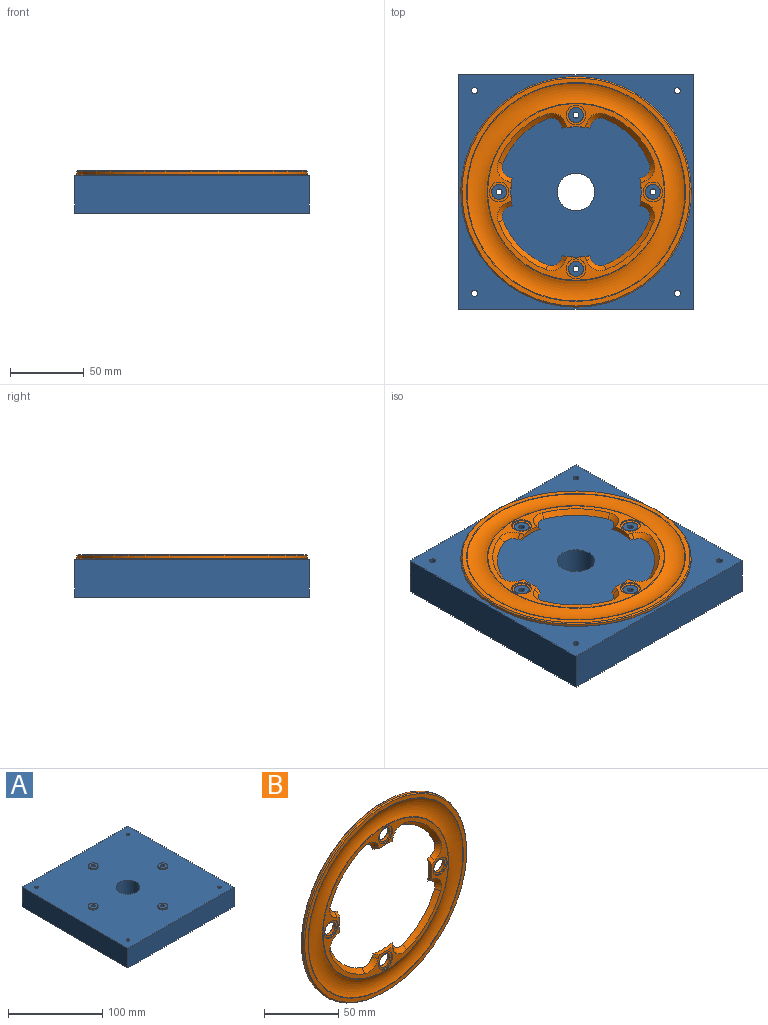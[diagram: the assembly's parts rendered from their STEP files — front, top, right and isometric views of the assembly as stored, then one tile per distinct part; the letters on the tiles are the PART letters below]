
ASSEMBLY  parts=2 mates=1
PART A: 23 faces, bbox 158.8x158.8x27.3 mm
  f0: plane 158.75x25.4mm, normal (-1,0,0), area 4032.3mm2, adj f1,f3,f4,f5
  f1: plane 158.75x25.4mm, normal (0,-1,0), area 4032.3mm2, adj f0,f2,f4,f5
  f2: plane 158.75x25.4mm, normal (1,0,0), area 4032.3mm2, adj f1,f3,f4,f5
  f3: plane 158.75x25.4mm, normal (0,1,0), area 4032.3mm2, adj f0,f2,f4,f5
  f4: plane 158.75x158.75mm, normal (0,0,-1), area 24592.4mm2, adj f0,f1,f2,f3,f14,f15,f16,f17
  f5: plane 158.75x158.75mm, normal (0,0,1), area 24320.9mm2, adj f0,f1,f2,f3,f6,f8,f10,f12
  f6: cylinder r=5.07mm len=10.13mm, axis (0,0,-1), area 60.7mm2, adj f5,f7
  f7: plane 10.13x10.13mm, normal (0,0,1), area 67.9mm2, adj f6,f17
  f8: cylinder r=5.07mm len=10.13mm, axis (0,0,-1), area 60.7mm2, adj f5,f9
  f9: plane 10.13x10.13mm, normal (0,0,1), area 67.9mm2, adj f8,f16
  f10: cylinder r=5.07mm len=10.13mm, axis (0,0,-1), area 60.7mm2, adj f5,f11
  f11: plane 10.13x10.13mm, normal (0,0,1), area 67.9mm2, adj f10,f15
  f12: cylinder r=5.07mm len=10.13mm, axis (0,0,-1), area 60.7mm2, adj f5,f13
  f13: plane 10.13x10.13mm, normal (0,0,1), area 67.9mm2, adj f12,f14
  f14: cylinder r=2.02mm len=27.31mm, axis (0,0,1), area 346.4mm2, adj f4,f13
  f15: cylinder r=2.02mm len=27.31mm, axis (0,0,1), area 346.4mm2, adj f4,f11
  f16: cylinder r=2.02mm len=27.31mm, axis (0,0,1), area 346.4mm2, adj f4,f9
  f17: cylinder r=2.02mm len=27.31mm, axis (0,0,1), area 346.4mm2, adj f4,f7
  f18: cylinder r=2.02mm len=25.4mm, axis (0,0,-1), area 322.3mm2, adj f4,f5
  f19: cylinder r=2.02mm len=25.4mm, axis (0,0,-1), area 322.3mm2, adj f4,f5
  f20: cylinder r=2.02mm len=25.4mm, axis (0,0,-1), area 322.3mm2, adj f4,f5
  f21: cylinder r=2.02mm len=25.4mm, axis (0,0,-1), area 322.3mm2, adj f4,f5
  f22: cylinder r=12.7mm len=25.4mm, axis (0,0,-1), area 2026.8mm2, adj f4,f5
PART B: 45 faces, bbox 168.7x6.1x168.7 mm
  f0: cylinder r=5.08mm len=10.16mm, axis (0,-1,0), area 72.2mm2, adj f6,f41
  f1: cylinder r=5.08mm len=10.16mm, axis (0,-1,0), area 72.2mm2, adj f6,f39
  f2: cylinder r=5.08mm len=10.16mm, axis (0,-1,0), area 72.2mm2, adj f6,f37
  f3: cylinder r=5.08mm len=10.16mm, axis (0,-1,0), area 72.2mm2, adj f6,f35
  f4: plane 154.31x154.31mm, normal (0,-1,0), area 1483.8mm2, adj f34,f44
  f5: plane 119.41x119.41mm, normal (0,-1,0), area 1629.6mm2, adj f8,f9,f10,f11,f13,f14,f15,f16
  f6: plane 154.31x154.31mm, normal (0,1,0), area 10363.6mm2, adj f0,f1,f2,f3,f8,f9,f10,f11
  f7: cylinder r=77.91mm len=155.83mm, axis (0,1,0), area 808.2mm2, adj f33,f34
  f8: cylinder r=44.13mm len=18.43mm, axis (0,-1,0), area 48.7mm2, adj f5,f6,f13,f32
  f9: cylinder r=44.13mm len=18.43mm, axis (0,-1,0), area 48.7mm2, adj f5,f6,f27,f28
  f10: cylinder r=44.13mm len=18.43mm, axis (0,-1,0), area 48.7mm2, adj f5,f6,f22,f23
  f11: cylinder r=44.13mm len=18.43mm, axis (0,-1,0), area 48.7mm2, adj f5,f6,f17,f18
  f12: torus R=66.87mm, axis (0,1,0), area 5939.5mm2, adj f43,f44
  f13: plane 4.02x3.4mm, normal (0.66,-0.71,-0.24), area 12.2mm2, adj f5,f6,f8,f14
  f14: cone r=6.35mm half-angle=45deg, axis (0,-1,0), area 61.2mm2, adj f5,f6,f13,f15
  f15: cone r=52.51mm half-angle=45deg, axis (0,-1,0), area 205.1mm2, adj f5,f6,f14,f16
  f16: cone r=10.16mm half-angle=45deg, axis (0,-1,0), area 61.2mm2, adj f5,f6,f15,f17
  f17: plane 4.02x3.4mm, normal (-0.24,-0.71,0.66), area 12.2mm2, adj f5,f6,f11,f16
  f18: plane 4.02x3.4mm, normal (-0.24,-0.71,-0.66), area 12.2mm2, adj f5,f6,f11,f19
  f19: cone r=6.35mm half-angle=45deg, axis (0,-1,0), area 61.2mm2, adj f5,f6,f18,f20
  f20: cone r=52.51mm half-angle=45deg, axis (0,-1,0), area 205.1mm2, adj f5,f6,f19,f21
  f21: cone r=10.16mm half-angle=45deg, axis (0,-1,0), area 61.2mm2, adj f5,f6,f20,f22
  f22: plane 4.02x3.4mm, normal (0.66,-0.71,0.24), area 12.2mm2, adj f5,f6,f10,f21
  f23: plane 4.02x3.4mm, normal (-0.66,-0.71,0.24), area 12.2mm2, adj f5,f6,f10,f24
  f24: cone r=6.35mm half-angle=45deg, axis (0,-1,0), area 61.2mm2, adj f5,f6,f23,f25
  f25: cone r=52.51mm half-angle=45deg, axis (0,-1,0), area 205.1mm2, adj f5,f6,f24,f26
  f26: cone r=10.16mm half-angle=45deg, axis (0,-1,0), area 61.2mm2, adj f5,f6,f25,f27
  f27: plane 4.02x3.4mm, normal (0.24,-0.71,-0.66), area 12.2mm2, adj f5,f6,f9,f26
  f28: plane 4.02x3.4mm, normal (0.24,-0.71,0.66), area 12.2mm2, adj f5,f6,f9,f29
  f29: cone r=6.35mm half-angle=45deg, axis (0,-1,0), area 61.2mm2, adj f5,f6,f28,f30
  f30: cone r=52.51mm half-angle=45deg, axis (0,-1,0), area 205.1mm2, adj f5,f6,f29,f31
  f31: cone r=10.16mm half-angle=45deg, axis (0,-1,0), area 61.2mm2, adj f5,f6,f30,f32
  f32: plane 4.02x3.4mm, normal (-0.66,-0.71,-0.24), area 12.2mm2, adj f5,f6,f8,f31
  f33: cone r=77.91mm half-angle=45deg, axis (0,-1,0), area 525mm2, adj f6,f7
  f34: cone r=77.15mm half-angle=45deg, axis (0,1,0), area 525mm2, adj f4,f7
  f35: plane 13.36x13.36mm, normal (0,-1,0), area 59.1mm2, adj f3,f36
  f36: cylinder r=6.68mm len=13.36mm, axis (0,-1,0), area 38.4mm2, adj f5,f35
  f37: plane 13.36x13.36mm, normal (0,-1,0), area 59.1mm2, adj f2,f38
  f38: cylinder r=6.68mm len=13.36mm, axis (0,-1,0), area 38.4mm2, adj f5,f37
  f39: plane 13.36x13.36mm, normal (0,-1,0), area 59.1mm2, adj f1,f40
  f40: cylinder r=6.68mm len=13.36mm, axis (0,-1,0), area 38.4mm2, adj f5,f39
  f41: plane 13.36x13.36mm, normal (0,-1,0), area 59.1mm2, adj f0,f42
  f42: cylinder r=6.68mm len=13.36mm, axis (0,-1,0), area 38.4mm2, adj f5,f41
  f43: torus R=59.7mm, axis (0,1,0), area 129.9mm2, adj f5,f12
  f44: torus R=74.03mm, axis (0,-1,0), area 160.2mm2, adj f4,f12
PLACE A t=(-6.56,-36.92,-21.05)mm
PLACE B rot(axis=(-1,0,0),90deg) t=(-6.56,-36.92,-21.05)mm
MATE fastened B.f25 <-> A.f22  axis (0,0,-1) through (-6.56,-36.92,-21.05)mm
